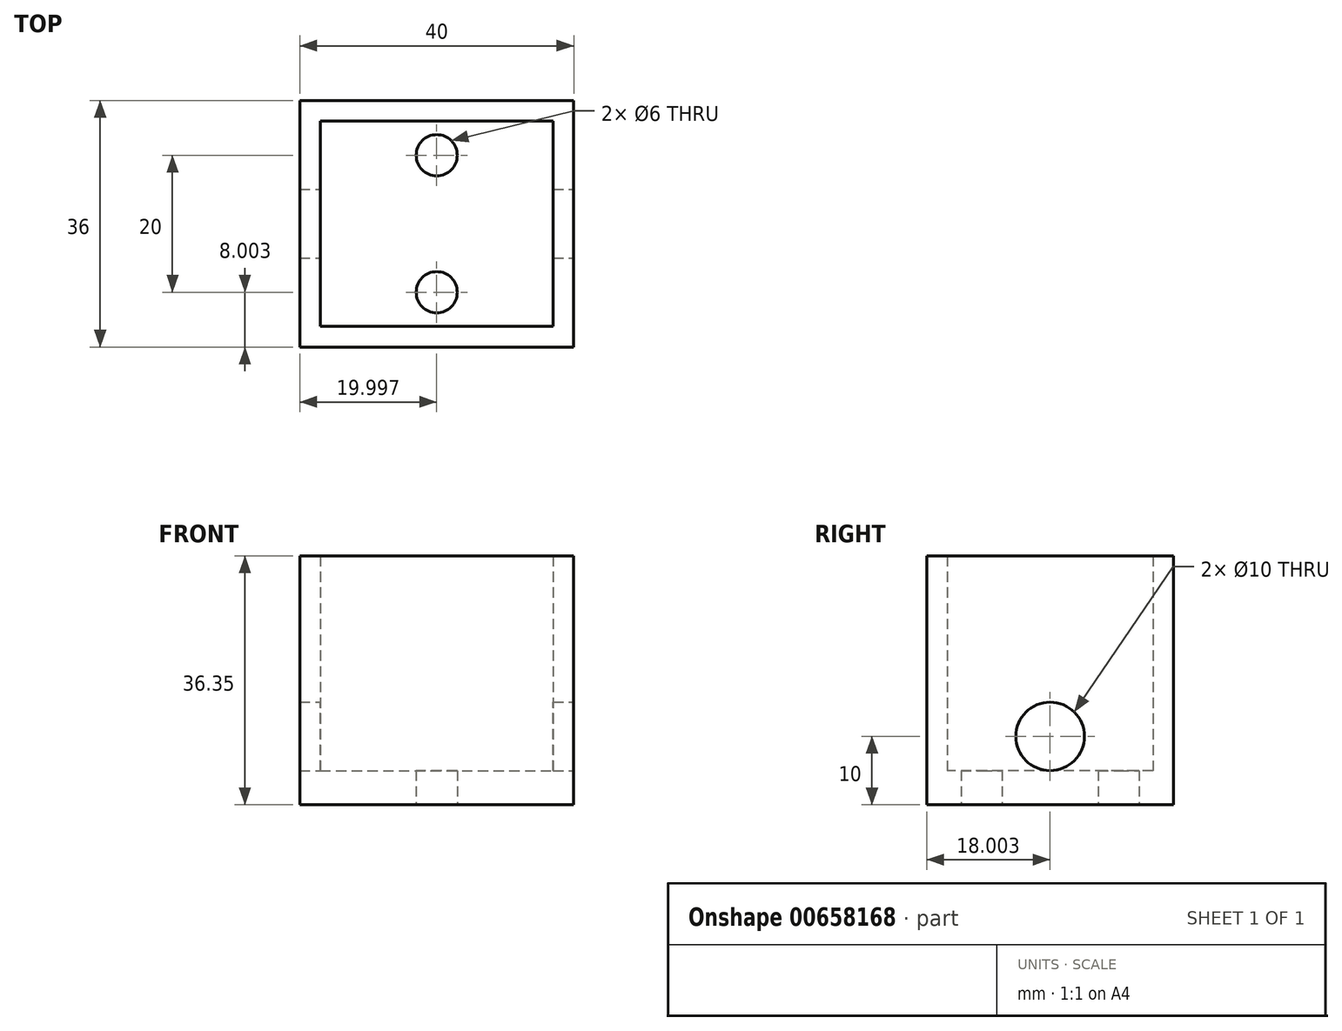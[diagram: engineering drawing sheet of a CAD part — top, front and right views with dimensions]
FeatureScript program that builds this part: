
annotation { "Feature Type Name" : "Feature", "Feature Type Description" : "" }
export const myFeature = defineFeature(function(context is Context, id is Id, definition is map)
    precondition{}
    {
        {
            var Q0;
            Q0=qCreatedBy(makeId("Top.planeOp"),FACE);
            var sketch = newSketch(context, id + "F0", { "sketchPlane" : qUnion([Q0])});
            skLineSegment(sketch, "E0.bottom", {"start": v(-16.98, 23.51) * mm, "end": v(23.02, 23.51) * mm});
            skLineSegment(sketch, "E0.top", {"start": v(-16.98, -12.49) * mm, "end": v(23.02, -12.49) * mm});
            skLineSegment(sketch, "E0.left", {"start": v(-16.98, 23.51) * mm, "end": v(-16.98, -12.49) * mm});
            skLineSegment(sketch, "E0.right", {"start": v(23.02, 23.51) * mm, "end": v(23.02, -12.49) * mm});
            skLineSegment(sketch, "E1.bottom", {"start": v(-13.98, 20.51) * mm, "end": v(20.02, 20.51) * mm});
            skLineSegment(sketch, "E1.top", {"start": v(-13.98, -9.49) * mm, "end": v(20.02, -9.49) * mm});
            skLineSegment(sketch, "E1.left", {"start": v(-13.98, 20.51) * mm, "end": v(-13.98, -9.49) * mm});
            skLineSegment(sketch, "E1.right", {"start": v(20.02, 20.51) * mm, "end": v(20.02, -9.49) * mm});
            skCircle(sketch, "E2", {"center": v(3.02, 15.51) * mm, "radius": 3 * mm});
            skCircle(sketch, "E3", {"center": v(3.02, -4.49) * mm, "radius": 3 * mm});
            skSolve(sketch);
        }
        {
            var Q0;
            Q0=makeQuery(id+"F0.imprint","IMPRINT",FACE,{"disambiguationData":[TD([[makeQuery(id+"F0.imprint","IMPRINT",EDGE,{"derivedFrom":sQuery(id+"F0.wireOp",EDGE,"E0.bottom")}),-1.0]])]});
            extrude(context, id + "F1", {"entities" : qUnion([Q0]), "depth" : 36.35 * mm, "offsetDistance" : 25 * mm});
        }
        {
            var Q0;
            Q0 = qSketchRegion(id + "F0", true);
            var Q1;
            Q1=makeQuery(id+"F0.imprint","IMPRINT",FACE,{"disambiguationData":[TD([[makeQuery(id+"F0.imprint","IMPRINT",EDGE,{"derivedFrom":sQuery(id+"F0.wireOp",EDGE,"E1.bottom")}),-1.0]])]});
            extrude(context, id + "F2", {"entities" : qUnion([Q0, Q1]), "operationType" : NewBodyOperationType.ADD, "depth" : 5 * mm, "offsetDistance" : 25 * mm});
        }
        {
            var Q0;
            Q0=makeQuery(id+"F1.opExtrude","SWEPT_FACE",FACE,{"disambiguationData":[OSD([sQuery(id+"F0.wireOp",EDGE,"E0.right")])]});
            var sketch = newSketch(context, id + "F3", { "sketchPlane" : qUnion([Q0])});
            skCircle(sketch, "E4", {"center": v(5.51, 10) * mm, "radius": 5 * mm});
            skSolve(sketch);
        }
        {
            var Q0;
            Q0=makeQuery(id+"F3.imprint","IMPRINT",FACE,{"disambiguationData":[TD([[makeQuery(id+"F3.imprint","IMPRINT",EDGE,{"derivedFrom":sQuery(id+"F3.wireOp",EDGE,"E4")}),1.0]])]});
            extrude(context, id + "F4", {"entities" : qUnion([Q0]), "operationType" : NewBodyOperationType.REMOVE, "endBound" : BoundingType.THROUGH_ALL, "oppositeDirection" : true, "depth" : 25 * mm, "offsetDistance" : 25 * mm});
        }
    });
